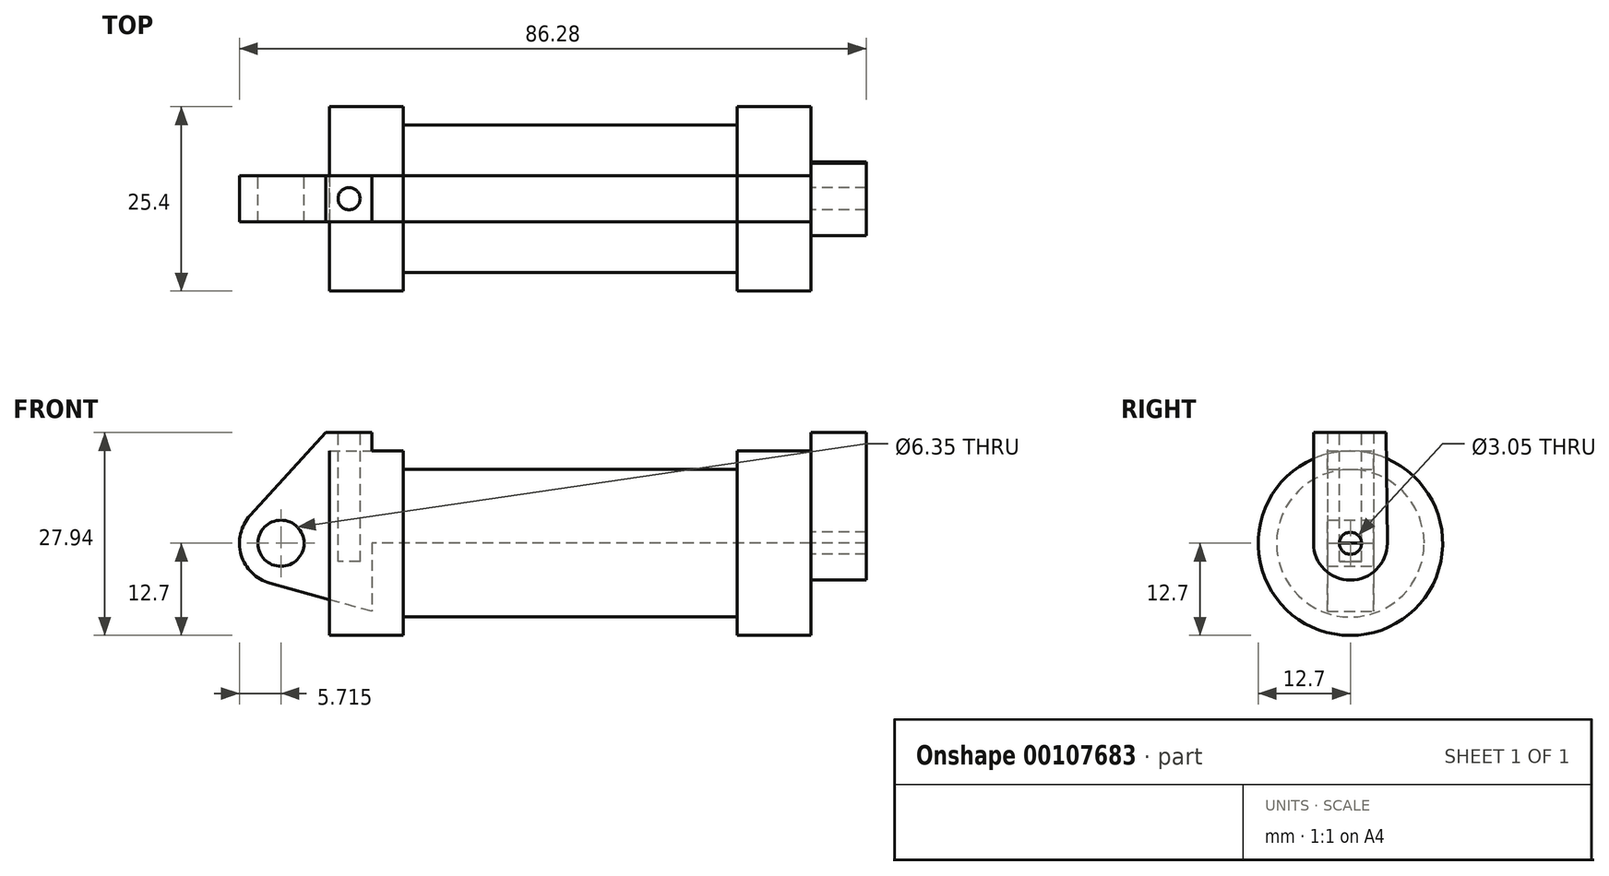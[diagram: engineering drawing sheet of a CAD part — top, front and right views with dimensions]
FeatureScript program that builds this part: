
annotation { "Feature Type Name" : "Feature", "Feature Type Description" : "" }
export const myFeature = defineFeature(function(context is Context, id is Id, definition is map)
    precondition{}
    {
        {
            var Q0;
            Q0=qCreatedBy(makeId("Front.planeOp"),FACE);
            var sketch = newSketch(context, id + "F0", { "sketchPlane" : qUnion([Q0])});
            skLineSegment(sketch, "E0", {"start": v(0, 0) * mm, "end": v(0, 12.7) * mm});
            skLineSegment(sketch, "E1", {"start": v(0, 12.7) * mm, "end": v(10.16, 12.7) * mm});
            skLineSegment(sketch, "E2", {"start": v(10.16, 12.7) * mm, "end": v(10.16, 10.16) * mm});
            skLineSegment(sketch, "E3", {"start": v(10.16, 10.16) * mm, "end": v(56.13, 10.16) * mm});
            skLineSegment(sketch, "E4", {"start": v(56.13, 10.16) * mm, "end": v(56.13, 12.7) * mm});
            skLineSegment(sketch, "E5", {"start": v(56.13, 12.7) * mm, "end": v(66.3, 12.7) * mm});
            skLineSegment(sketch, "E6", {"start": v(66.3, 12.7) * mm, "end": v(66.3, 0) * mm});
            skLineSegment(sketch, "E7", {"start": v(66.3, 0) * mm, "end": v(0, 0) * mm});
            skLineSegment(sketch, "E8", {"start": v(5.84, 15.24) * mm, "end": v(-0.5, 15.24) * mm});
            skLineSegment(sketch, "E9", {"start": v(-0.5, 15.24) * mm, "end": v(-10.88, 3.85) * mm});
            skLineSegment(sketch, "E10", {"start": v(0, 0) * mm, "end": v(-6.65, 0) * mm});
            skCircle(sketch, "E11", {"center": v(-6.65, 0) * mm, "radius": 5.72 * mm});
            skCircle(sketch, "E12", {"center": v(-6.65, 0) * mm, "radius": 3.18 * mm});
            skLineSegment(sketch, "E13", {"start": v(5.84, 15.24) * mm, "end": v(5.84, -9.4) * mm});
            skLineSegment(sketch, "E14", {"start": v(5.84, -9.4) * mm, "end": v(-8.18, -5.5) * mm});
            skSolve(sketch);
        }
        {
            var Q0;
            {var subQ0=sQuery(id+"F0.wireOp",EDGE,"E2");Q0=makeQuery(id+"F0.imprint","IMPRINT",FACE,{"disambiguationData":[TD([[makeQuery(id+"F0.imprint","IMPRINT",EDGE,{"derivedFrom":subQ0}),-1.0]])]});}
            var Q1;
            {var subQ0=sQuery(id+"F0.wireOp",EDGE,"E0");Q1=makeQuery(id+"F0.imprint","IMPRINT",FACE,{"disambiguationData":[TD([[makeQuery(id+"F0.imprint","IMPRINT",EDGE,{"derivedFrom":subQ0}),-1.0]])]});}
            var Q2;
            Q2=sQuery(id+"F0.wireOp",EDGE,"E7");
            revolve(context, id + "F1", {"entities" : qUnion([Q0, Q1]), "axis" : qUnion([Q2]), "revolveType" : RevolveType.FULL});
        }
        {
            var Q0;
            Q0 = qSketchRegion(id + "F0", true);
            extrude(context, id + "F2", {"entities" : qUnion([Q0]), "endBound" : BoundingType.SYMMETRIC, "depth" : 6.35 * mm});
        }
        {
            var Q0;
            Q0=makeQuery(id+"F1.opRevolve","SWEPT_FACE",FACE,{"disambiguationData":[OSD([sQuery(id+"F0.wireOp",EDGE,"E6")])]});
            var sketch = newSketch(context, id + "F3", { "sketchPlane" : qUnion([Q0])});
            skCircle(sketch, "E15", {"center": v(0, 0) * mm, "radius": 1.52 * mm});
            skCircle(sketch, "E16", {"center": v(0, 0) * mm, "radius": 5.08 * mm});
            skLineSegment(sketch, "E17", {"start": v(-5.08, 0) * mm, "end": v(-5.08, 15.24) * mm});
            skLineSegment(sketch, "E18", {"start": v(-5.08, 15.24) * mm, "end": v(4.9, 15.24) * mm});
            skLineSegment(sketch, "E19", {"start": v(4.9, 15.24) * mm, "end": v(5.08, 0) * mm});
            skSolve(sketch);
        }
        {
            var Q0;
            {var subQ0=sQuery(id+"F3.wireOp",EDGE,"E17");var subQ1=sQuery(id+"F3.wireOp",EDGE,"E16");var subQ2=makeQuery(id+"F3.imprint","INTERSECT",VERTEX,{"derivedFrom":[subQ1,subQ0]});Q0=makeQuery(id+"F3.imprint","IMPRINT",FACE,{"disambiguationData":[TD([[makeQuery(id+"F3.imprint","IMPRINT",EDGE,{"disambiguationData":[TD([[subQ2,1.0]])],"derivedFrom":subQ1}),-1.0]])]});}
            var Q1;
            {var subQ0=sQuery(id+"F3.wireOp",EDGE,"E18");Q1=makeQuery(id+"F3.imprint","IMPRINT",FACE,{"disambiguationData":[TD([[makeQuery(id+"F3.imprint","IMPRINT",EDGE,{"derivedFrom":subQ0}),-1.0]])]});}
            var Q2;
            Q2=makeQuery(id+"F3.imprint","IMPRINT",FACE,{"disambiguationData":[TD([[makeQuery(id+"F3.imprint","IMPRINT",EDGE,{"derivedFrom":sQuery(id+"F3.wireOp",EDGE,"E15")}),-1.0]])]});
            extrude(context, id + "F4", {"entities" : qUnion([Q0, Q1, Q2]), "depth" : 7.62 * mm});
        }
        {
            var Q0;
            Q0=makeQuery(id+"F2.opExtrude","SWEPT_FACE",FACE,{"disambiguationData":[OSD([sQuery(id+"F0.wireOp",EDGE,"E8")])]});
            var sketch = newSketch(context, id + "F5", { "sketchPlane" : qUnion([Q0])});
            skCircle(sketch, "E20", {"center": v(69.7, 0.13) * mm, "radius": 1.52 * mm});
            skSolve(sketch);
        }
        {
            var Q0;
            {var subQ0=sQuery(id+"F0.wireOp",EDGE,"E8");Q0=makeQuery(id+"F5.imprint","IMPRINT",FACE,{"disambiguationData":[TD([[makeQuery(id+"F5.imprint","IMPRINT",EDGE,{"derivedFrom":makeQuery(id+"F2.opExtrude","CAP_EDGE",EDGE,{"disambiguationData":[OSD([subQ0])],"isStart":true})}),1.0]])]});}
            var sketch = newSketch(context, id + "F6", { "sketchPlane" : qUnion([Q0])});
            skCircle(sketch, "E21", {"center": v(2.72, 0.04) * mm, "radius": 1.52 * mm});
            skSolve(sketch);
        }
        {
            var Q0;
            Q0=makeQuery(id+"F6.imprint","IMPRINT",FACE,{"disambiguationData":[TD([[makeQuery(id+"F6.imprint","IMPRINT",EDGE,{"derivedFrom":sQuery(id+"F6.wireOp",EDGE,"E21")}),1.0]])]});
            extrude(context, id + "F7", {"entities" : qUnion([Q0]), "oppositeDirection" : true, "depth" : 17.78 * mm});
        }
        {
            var Q0;
            Q0=makeQuery(id+"F5.imprint","IMPRINT",FACE,{"disambiguationData":[TD([[makeQuery(id+"F5.imprint","IMPRINT",EDGE,{"derivedFrom":sQuery(id+"F5.wireOp",EDGE,"E20")}),1.0]])]});
            extrude(context, id + "F8", {"entities" : qUnion([Q0]), "operationType" : NewBodyOperationType.ADD, "oppositeDirection" : true, "depth" : 10.4 * mm});
        }
    });
